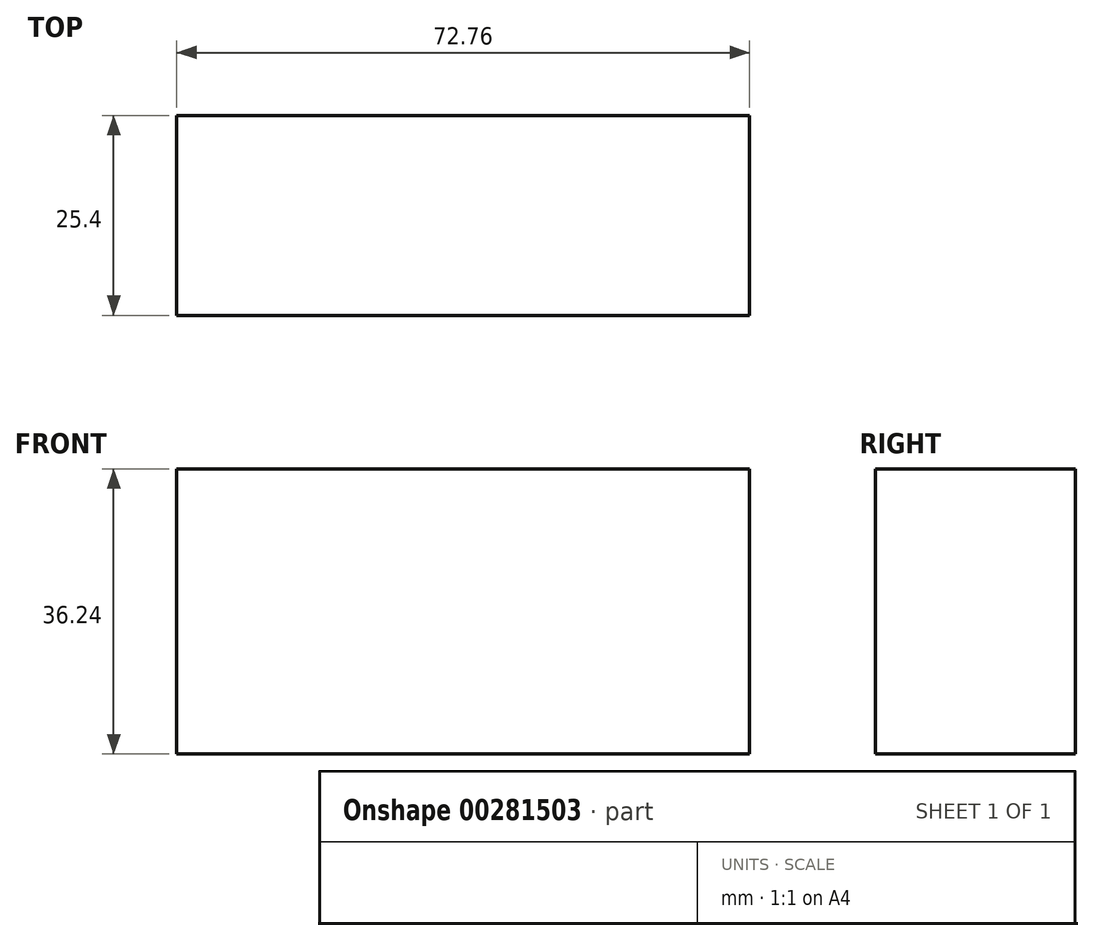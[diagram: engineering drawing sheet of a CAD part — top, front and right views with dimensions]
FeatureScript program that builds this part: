
annotation { "Feature Type Name" : "Feature", "Feature Type Description" : "" }
export const myFeature = defineFeature(function(context is Context, id is Id, definition is map)
    precondition{}
    {
        {
            var Q0;
            Q0=qCreatedBy(makeId("Front.planeOp"),FACE);
            var sketch = newSketch(context, id + "F0", { "sketchPlane" : qUnion([Q0])});
            skLineSegment(sketch, "E0.bottom", {"start": v(-35.06, 18.16) * mm, "end": v(37.7, 18.16) * mm});
            skLineSegment(sketch, "E0.top", {"start": v(-35.06, -18.08) * mm, "end": v(37.7, -18.08) * mm});
            skLineSegment(sketch, "E0.left", {"start": v(-35.06, 18.16) * mm, "end": v(-35.06, -18.08) * mm});
            skLineSegment(sketch, "E0.right", {"start": v(37.7, 18.16) * mm, "end": v(37.7, -18.08) * mm});
            skSolve(sketch);
        }
        {
            var Q0;
            Q0 = qSketchRegion(id + "F0", true);
            extrude(context, id + "F1", {"entities" : qUnion([Q0]), "depth" : 25.4 * mm});
        }
    });
